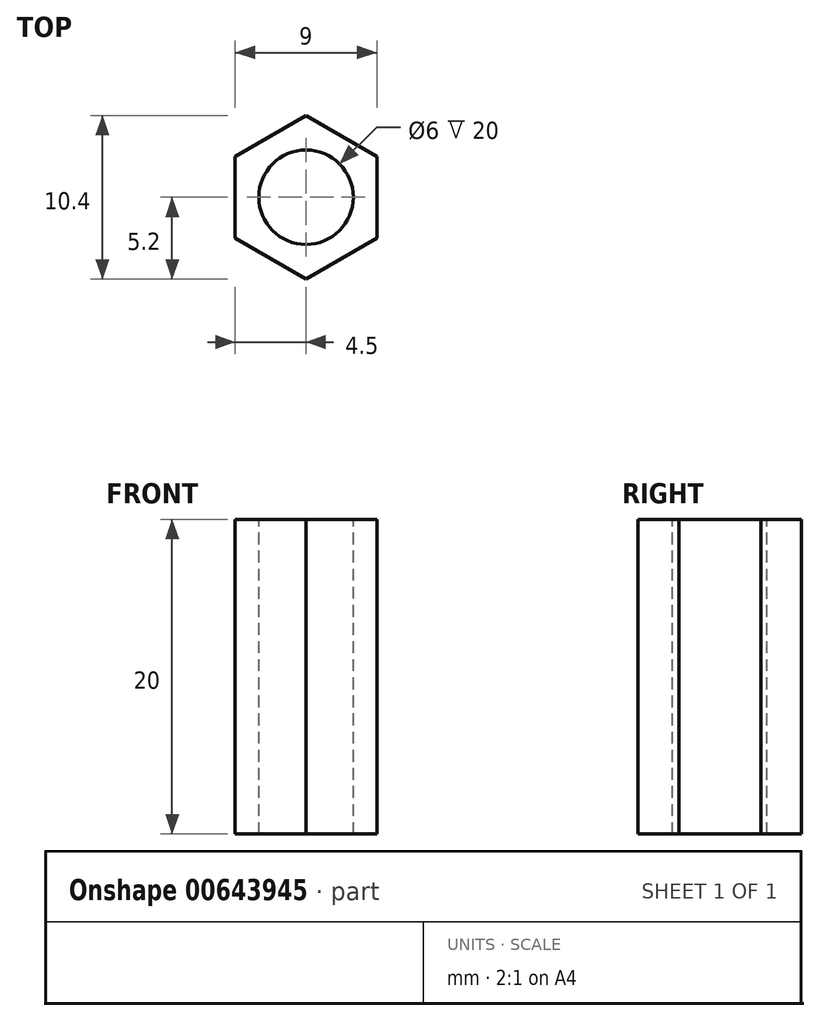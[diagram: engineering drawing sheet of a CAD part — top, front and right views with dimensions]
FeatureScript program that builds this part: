
annotation { "Feature Type Name" : "Feature", "Feature Type Description" : "" }
export const myFeature = defineFeature(function(context is Context, id is Id, definition is map)
    precondition{}
    {
        {
            var Q0;
            Q0=qCreatedBy(makeId("Top.planeOp"),FACE);
            var sketch = newSketch(context, id + "F0", { "sketchPlane" : qUnion([Q0])});
            skCircle(sketch, "E0.cCircle", {"center": v(0, 0) * mm, "radius": 5.2 * mm, "construction": true});
            skLineSegment(sketch, "E0.0", {"start": v(0, 5.2) * mm, "end": v(4.5, 2.6) * mm});
            skLineSegment(sketch, "E0.1", {"start": v(4.5, 2.6) * mm, "end": v(4.5, -2.6) * mm});
            skLineSegment(sketch, "E0.2", {"start": v(4.5, -2.6) * mm, "end": v(0, -5.2) * mm});
            skLineSegment(sketch, "E0.3", {"start": v(0, -5.2) * mm, "end": v(-4.5, -2.6) * mm});
            skLineSegment(sketch, "E0.4", {"start": v(-4.5, -2.6) * mm, "end": v(-4.5, 2.6) * mm});
            skLineSegment(sketch, "E0.5", {"start": v(-4.5, 2.6) * mm, "end": v(0, 5.2) * mm});
            skSolve(sketch);
        }
        {
            var Q0;
            Q0=makeQuery(id+"F0.imprint","IMPRINT",FACE,{"disambiguationData":[TD([[makeQuery(id+"F0.imprint","IMPRINT",EDGE,{"derivedFrom":sQuery(id+"F0.wireOp",EDGE,"E0.0")}),-1.0]])]});
            extrude(context, id + "F1", {"entities" : qUnion([Q0]), "depth" : 20 * mm, "offsetDistance" : 25 * mm});
        }
        {
            var Q0;
            Q0=makeQuery(id+"F1.opExtrude","CAP_FACE",FACE,{"disambiguationData":[OSD([sQuery(id+"F0.wireOp",EDGE,"E0.0"),sQuery(id+"F0.wireOp",EDGE,"E0.1"),sQuery(id+"F0.wireOp",EDGE,"E0.2"),sQuery(id+"F0.wireOp",EDGE,"E0.3"),sQuery(id+"F0.wireOp",EDGE,"E0.4"),sQuery(id+"F0.wireOp",EDGE,"E0.5")])],"isStart":false});
            var sketch = newSketch(context, id + "F2", { "sketchPlane" : qUnion([Q0])});
            skCircle(sketch, "E1", {"center": v(0, 0) * mm, "radius": 3 * mm});
            skSolve(sketch);
        }
        {
            var Q0;
            Q0=makeQuery(id+"F2.imprint","IMPRINT",FACE,{"disambiguationData":[TD([[makeQuery(id+"F2.imprint","IMPRINT",EDGE,{"derivedFrom":sQuery(id+"F2.wireOp",EDGE,"E1")}),1.0]])]});
            extrude(context, id + "F3", {"entities" : qUnion([Q0]), "operationType" : NewBodyOperationType.REMOVE, "oppositeDirection" : true, "depth" : 20 * mm, "offsetDistance" : 25 * mm});
        }
    });
